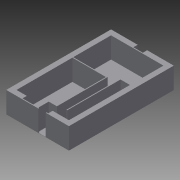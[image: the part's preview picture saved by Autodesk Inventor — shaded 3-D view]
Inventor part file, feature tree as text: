
AUTODESK INVENTOR PART (.ipt)
format: ipt  version: 2014 (Build 180170000, 170)  size: 268,288 bytes
history: native  units: in
note: dims shown in document units (in); Inventor stores cm internally (conversion verified against a paired STEP export)
features: extrude x6, sketch x6, projected_geometry x2
ambient origin geometry x8: Origin, YZ Plane, XZ Plane, XY Plane, X Axis, Y Axis, Z Axis, Center Point
bodies: Solid1 (feature_tree)
feature tree (14):
  extrude  "Extrusion1"  Depth=480.315in
  extrude  "Extrusion2"  Depth=456.6929in
  extrude  "Extrusion6"  Depth=118.1102in
  extrude  "Instrumentation"  Depth=98.4252in
  extrude  "Pallets"  Depth=433.0709in
  extrude  "Furniture"  Depth=157.4803in
  sketch  "Sketch1"  dims[d0=287.4016in d1=480.315in]
  sketch  "Sketch2"  dims[d2=240.1575in d4=456.6929in]
  projected_geometry  "Projected Loop1"
  sketch  "Sketch3"  dims[d5=74.8031in d6=118.1102in]
  sketch  "Sketch4"  dims[d7=98.4252in d8=98.4252in]
  sketch  "Sketch5"  dims[d9=480.315in d10=433.0709in]
  sketch  "Sketch6"  dims[d11=3.937in d12=157.4803in d14=3.937in d16=3.937in d17=3.937in d18=3.937in d19=7.874in d20=3.937in d22=47.2441in d23=255.9055in d24=3.937in d25=3.937in d26=47.2441in d27=149.6063in d28=3.937in d29=248.0315in d30=96.0in d31=0.0in d32=1.0in d33=0.0in d34=82.6772in d35=78.7402in d36=82.6772in d37=78.7402in d38=6.0in d39=6.0in d40=82.6772in d41=82.6772in d42=84.6457in d43=6.0in d44=6.0in d45=6.0in d46=84.6457in d49=6.0in d50=6.0in d51=23.622in d52=23.622in d53=6.0in d54=6.0in d56=86.6142in d57=98.4252in d59=23.622in d60=17.867in d61=17.867in d62=17.867in d63=6.0in d64=6.0in d65=6.0in d66=6.0in d73=3.0in d74=5.0in d75=5.0in d76=3.0in d77=6.0in d78=0.0in d79=39.3701in d80=47.2441in d81=47.2441in d82=7.874in d83=11.811in d84=11.811in d85=6.0in d86=0.0in d87=62.9921in d88=35.4331in d89=35.4331in d90=39.3701in d91=27.5591in d92=31.4961in d93=106.2992in d94=43.3071in d95=27.5591in d98=31.4961in d99=6.0in d100=0.0in d101=62.9921in d102=3.937in d103=1.0in d104=0.0in d107=6.0in d108=6.0in]
  projected_geometry  "Projected Loop2"
